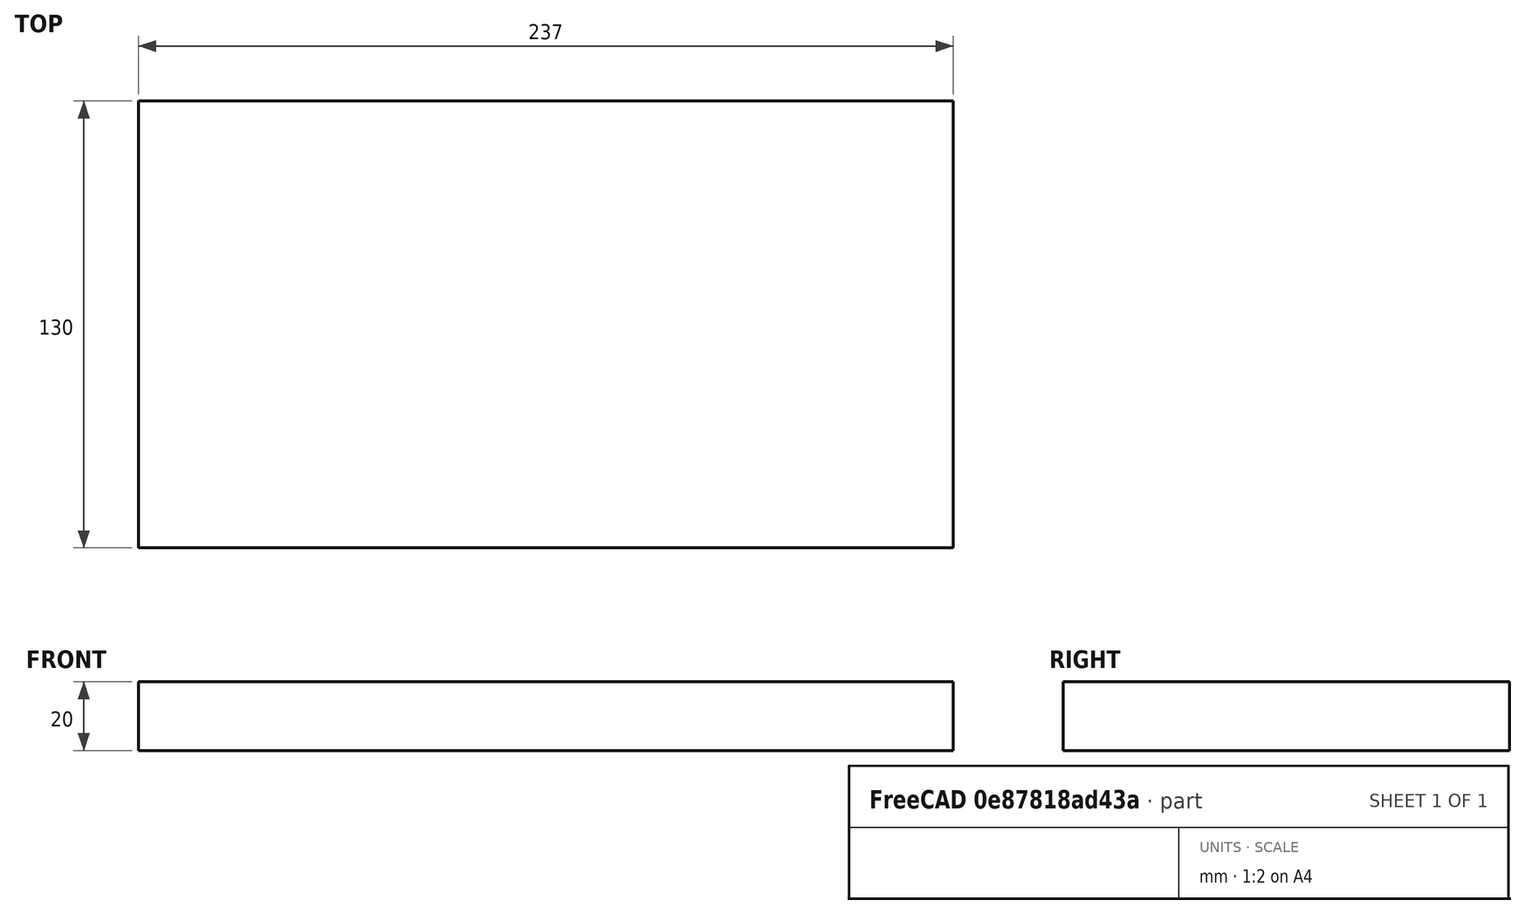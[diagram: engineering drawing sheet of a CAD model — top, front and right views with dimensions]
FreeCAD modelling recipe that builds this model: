
FCSTD DOCUMENT  (FreeCAD 1.0R39109 (Git))
Label: base
License: All rights reserved
LicenseURL: https://en.wikipedia.org/wiki/All_rights_reserved
objects: Sketcher::SketchObject×1, PartDesign::Body×1, Part::Extrusion×1
note: 4 computed .brp shape members not serialized (recipe doc carries the construction recipe); baked Part::Feature solids carry a one-line shape summary decoded from their .brp

FEATURE [Sketcher::SketchObject] Sketch
  ArcFitTolerance = 1e-06
  AttachmentSupport = -> [XY_Plane]
  FullyConstrained = true
  MakeInternals = false
  MapMode = 5
  sketch-geometry (5):
    g0: LineSegment StartX=-118.5 StartY=-65 StartZ=0 EndX=118.5 EndY=-65 EndZ=0
    g1: LineSegment StartX=118.5 StartY=-65 StartZ=0 EndX=118.5 EndY=65 EndZ=0
    g2: LineSegment StartX=118.5 StartY=65 StartZ=0 EndX=-118.5 EndY=65 EndZ=0
    g3: LineSegment StartX=-118.5 StartY=65 StartZ=0 EndX=-118.5 EndY=-65 EndZ=0
    g4: GeomPoint [constr] X=0 Y=0 Z=0
  constraints (12):
    c: Coincident(g0,g1)
    c: Coincident(g1,g2)
    c: Coincident(g2,g3)
    c: Coincident(g3,g0)
    c: Horizontal(g0)
    c: Horizontal(g2)
    c: Vertical(g1)
    c: Vertical(g3)
    c: Symmetric(g2,g0,g4)
    c: Distance(g1,g3) = 237
    c: Distance(g0,g2) = 130
    c: Coincident(g4,g-1)
FEATURE [PartDesign::Body] Body
  AllowCompound = false
  Group = -> [Sketch]
  Origin = -> Origin
FEATURE [Part::Extrusion] Extrude
  Base = -> Sketch
  Dir = (0,0,1)
  DirMode = 2
  FaceMakerClass = Part::FaceMakerBullseye
  FaceMakerMode = 3
  LengthFwd = 20
  LengthRev = 0
  Solid = true
  Symmetric = false
